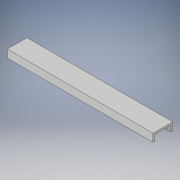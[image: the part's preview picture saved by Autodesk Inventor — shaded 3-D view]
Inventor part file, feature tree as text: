
AUTODESK INVENTOR PART (.ipt)
format: ipt  version: 2017 (Build 210142000, 142)  size: 97,792 bytes
history: native  units: in
note: dims shown in document units (in); Inventor stores cm internally (conversion verified against a paired STEP export)
features: extrude x1, sketch x1
ambient origin geometry x8: Origin, YZ Plane, XZ Plane, XY Plane, X Axis, Y Axis, Z Axis, Center Point
bodies: Solid1 (feature_tree)
feature tree (2):
  extrude  "Extrusion1"  Depth=2.5in
  sketch  "Sketch1"  dims[d0=1.0in d1=2.5in d2=2.0in d3=0.75in d4=0.25in d5=18.5in d6=0.0in]
